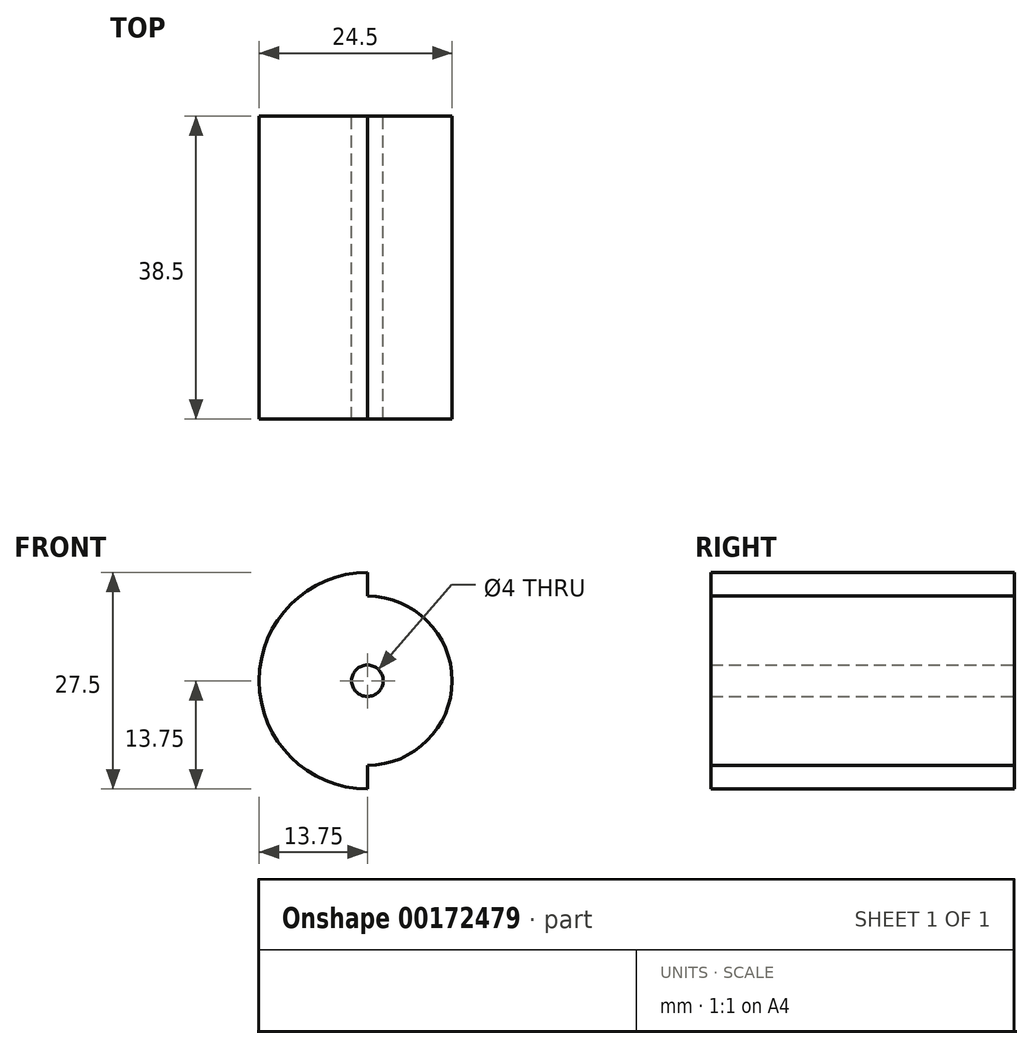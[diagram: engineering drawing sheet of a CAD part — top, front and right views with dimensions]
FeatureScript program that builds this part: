
annotation { "Feature Type Name" : "Feature", "Feature Type Description" : "" }
export const myFeature = defineFeature(function(context is Context, id is Id, definition is map)
    precondition{}
    {
        {
            var Q0;
            Q0=qCreatedBy(makeId("Front.planeOp"),FACE);
            var sketch = newSketch(context, id + "F0", { "sketchPlane" : qUnion([Q0])});
            skArc(sketch, "E0", {"start": v(0, 13.75) * mm, "mid": v(-13.75, 0) * mm, "end": v(0, -13.75) * mm});
            skArc(sketch, "E1", {"start": v(0, -10.75) * mm, "mid": v(10.75, 0) * mm, "end": v(0, 10.75) * mm});
            skLineSegment(sketch, "E2", {"start": v(0, 10.75) * mm, "end": v(0, 13.75) * mm});
            skLineSegment(sketch, "E3", {"start": v(0, -10.75) * mm, "end": v(0, -13.75) * mm});
            skCircle(sketch, "E4", {"center": v(0, 0) * mm, "radius": 2 * mm});
            skSolve(sketch);
        }
        {
            var Q0;
            Q0 = qSketchRegion(id + "F0", true);
            extrude(context, id + "F1", {"entities" : qUnion([Q0]), "depth" : 38.5 * mm, "symmetric" : true});
        }
    });
